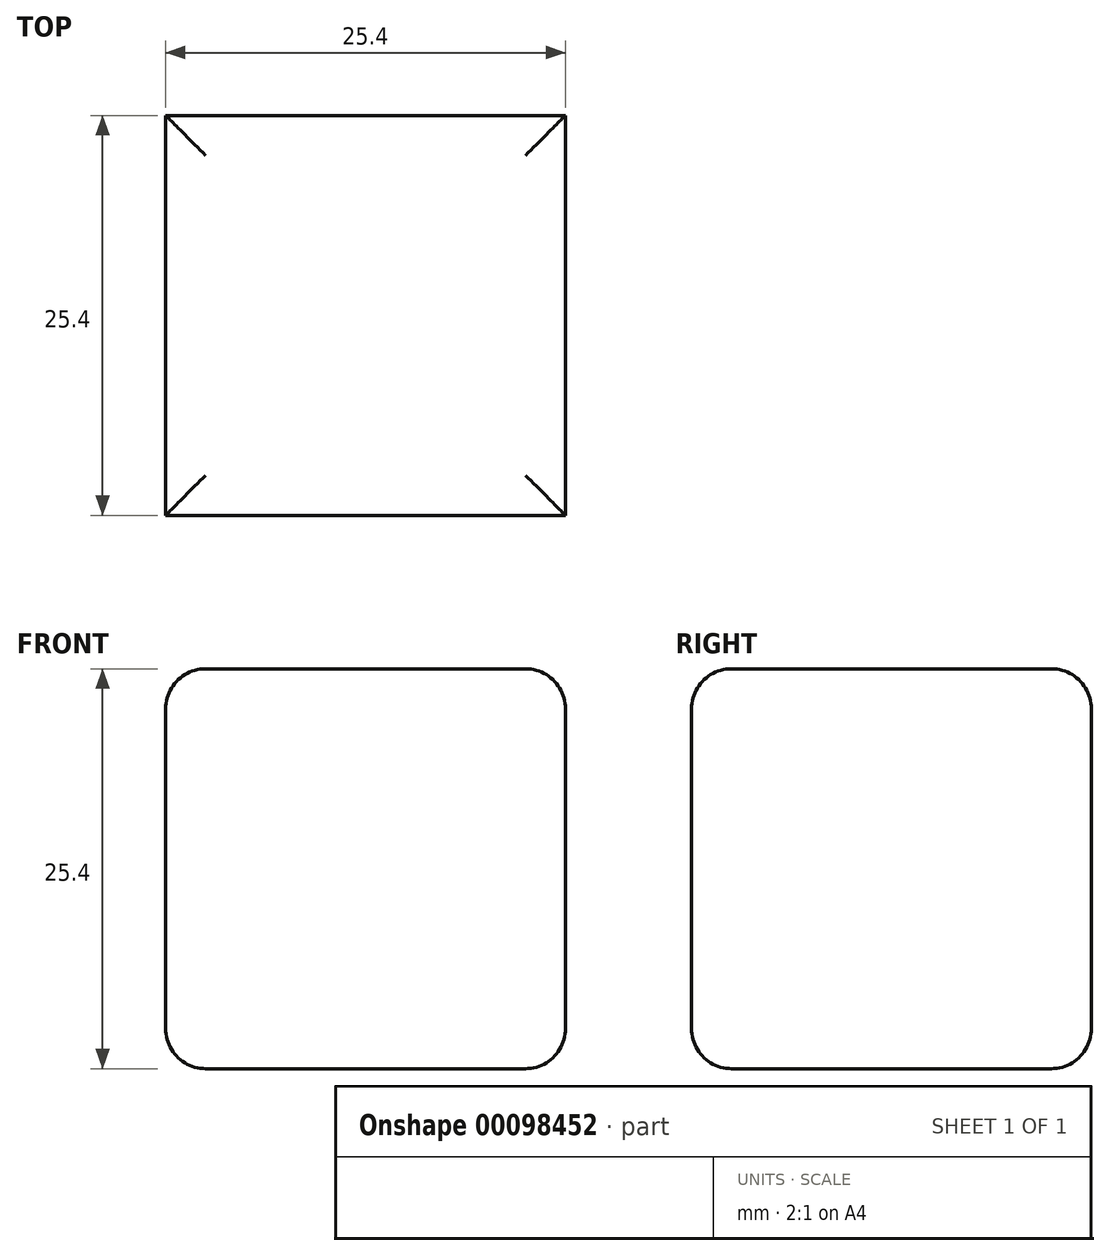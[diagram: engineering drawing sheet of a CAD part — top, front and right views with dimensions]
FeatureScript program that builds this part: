
annotation { "Feature Type Name" : "Feature", "Feature Type Description" : "" }
export const myFeature = defineFeature(function(context is Context, id is Id, definition is map)
    precondition{}
    {
        {
            var Q0;
            Q0=qCreatedBy(makeId("Top.planeOp"),FACE);
            var sketch = newSketch(context, id + "F0", { "sketchPlane" : qUnion([Q0])});
            skLineSegment(sketch, "E0.bottom", {"start": v(-12.7, 12.7) * mm, "end": v(12.7, 12.7) * mm});
            skLineSegment(sketch, "E0.top", {"start": v(-12.7, -12.7) * mm, "end": v(12.7, -12.7) * mm});
            skLineSegment(sketch, "E0.left", {"start": v(-12.7, 12.7) * mm, "end": v(-12.7, -12.7) * mm});
            skLineSegment(sketch, "E0.right", {"start": v(12.7, 12.7) * mm, "end": v(12.7, -12.7) * mm});
            skPoint(sketch, "E0.middle", {"position": v(0, 0) * mm});
            skSolve(sketch);
        }
        {
            var Q0;
            Q0=makeQuery(id+"F0.imprint","IMPRINT",FACE,{"disambiguationData":[TD([[makeQuery(id+"F0.imprint","IMPRINT",EDGE,{"derivedFrom":sQuery(id+"F0.wireOp",EDGE,"E0.bottom")}),-1.0]])]});
            extrude(context, id + "F1", {"entities" : qUnion([Q0]), "depth" : 25.4 * mm});
        }
        {
            assignVariable(context, id + "F2", {"name" : "BaseFillet", "anyValue" : 2.54 * mm});
        }
        {
            var Q0;
            Q0=makeQuery(id+"F1.opExtrude","CAP_FACE",FACE,{"disambiguationData":[OSD([sQuery(id+"F0.wireOp",EDGE,"E0.bottom"),sQuery(id+"F0.wireOp",EDGE,"E0.top"),sQuery(id+"F0.wireOp",EDGE,"E0.left"),sQuery(id+"F0.wireOp",EDGE,"E0.right")])],"isStart":false});
            fillet(context, id + "F3", {"entities" : qUnion([Q0]), "radius" : getVariable(context, 'BaseFillet'), "tangentPropagation" : true, "allowEdgeOverflow" : false});
        }
        {
            var Q0;
            Q0=makeQuery(id+"F1.opExtrude","CAP_FACE",FACE,{"disambiguationData":[OSD([sQuery(id+"F0.wireOp",EDGE,"E0.bottom"),sQuery(id+"F0.wireOp",EDGE,"E0.top"),sQuery(id+"F0.wireOp",EDGE,"E0.left"),sQuery(id+"F0.wireOp",EDGE,"E0.right")])],"isStart":true});
            fillet(context, id + "F4", {"entities" : qUnion([Q0]), "radius" : getVariable(context, 'BaseFillet'), "tangentPropagation" : true, "allowEdgeOverflow" : false});
        }
    });
